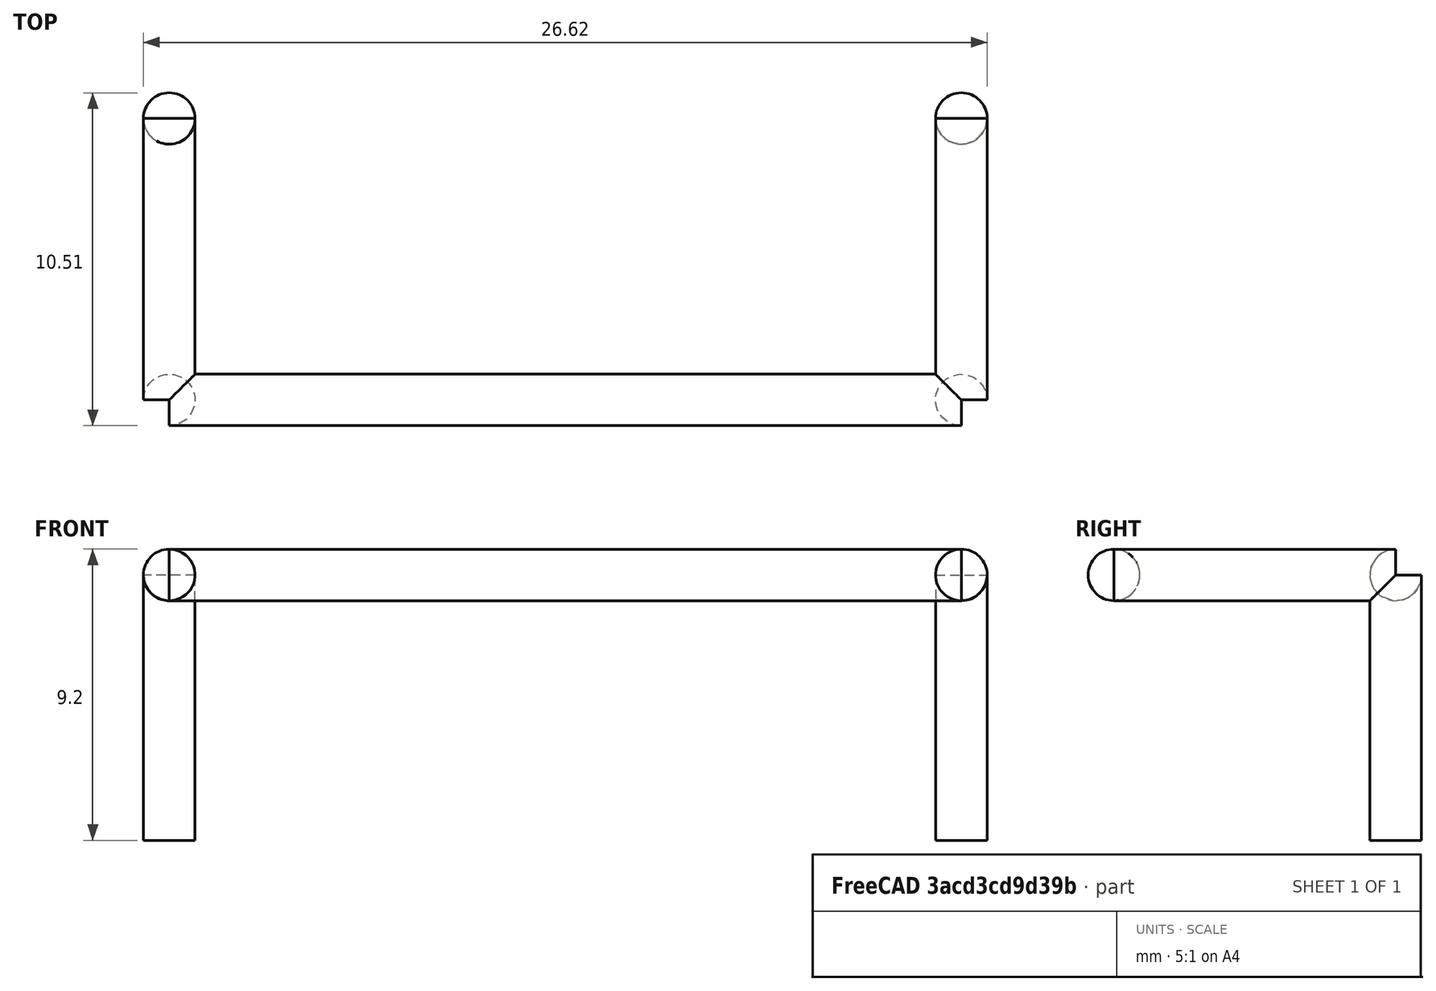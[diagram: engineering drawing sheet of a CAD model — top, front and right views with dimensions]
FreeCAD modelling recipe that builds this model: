
FCSTD DOCUMENT  (FreeCAD 1.0R39319 (Git))
Label: Wire Jumper
License: All rights reserved
LicenseURL: https://en.wikipedia.org/wiki/All_rights_reserved
objects: Sketcher::SketchObject×3, PartDesign::Plane×1, PartDesign::SubShapeBinder×1, PartDesign::AdditivePipe×1, PartDesign::Body×1
note: 12 computed .brp shape members not serialized (recipe doc carries the construction recipe); baked Part::Feature solids carry a one-line shape summary decoded from their .brp

FEATURE [Sketcher::SketchObject] Sketch
  ArcFitTolerance = 1e-06
  AttachmentSupport = -> [XZ_Plane]
  FullyConstrained = true
  MakeInternals = false
  MapMode = 5
  Placement = pos=(0,0,0) rot=(1,0,0;1.5708rad)
  sketch-geometry (2):
    g0: LineSegment StartX=-12.5 StartY=0 StartZ=0 EndX=-12.5 EndY=8.382 EndZ=0
    g1: LineSegment StartX=12.5 StartY=1e-16 StartZ=0 EndX=12.5 EndY=8.382 EndZ=0
  constraints (7):
    c: PointOnObject(g0,g-1)
    c: Vertical(g0)
    c: Vertical(g1)
    c: Symmetric(g0,g1,g-2)
    c: Distance(g1,g0) = 25
    c: Equal(g1,g0)
    c: DistanceY(g1,g1) = 8.382
FEATURE [PartDesign::Plane] DatumPlane
  AttachmentOffset = pos=(0,0,8.382) rot=(0,0,1;0rad)
  AttachmentSupport = -> [XY_Plane]
  Length = 60
  MapMode = 5
  Placement = pos=(0,0,8.382) rot=(0,0,1;0rad)
  ResizeMode = 0
  Width = 60
FEATURE [Sketcher::SketchObject] Sketch001
  ArcFitTolerance = 1e-06
  AttachmentSupport = -> [DatumPlane]
  FullyConstrained = true
  MakeInternals = false
  MapMode = 5
  Placement = pos=(0,0,8.382) rot=(0,0,1;0rad)
  sketch-geometry (3):
    g0: LineSegment StartX=-12.5 StartY=0 StartZ=0 EndX=-12.5 EndY=-8.89 EndZ=0
    g1: LineSegment StartX=-12.5 StartY=-8.89 StartZ=0 EndX=12.5 EndY=-8.89 EndZ=0
    g2: LineSegment StartX=12.5 StartY=-8.89 StartZ=0 EndX=12.5 EndY=0 EndZ=0
  constraints (9):
    c: PointOnObject(g0,g-1)
    c: Vertical(g0)
    c: Coincident(g1,g0)
    c: Coincident(g2,g1)
    c: Vertical(g2)
    c: PointOnObject(g2,g-1)
    c: Symmetric(g1,g0,g-2)
    c: DistanceX(g1,g1) = 25
    c: DistanceY(g2,g2) = 8.89
FEATURE [Sketcher::SketchObject] Sketch002
  ArcFitTolerance = 1e-06
  AttachmentSupport = -> [XY_Plane]
  FullyConstrained = true
  MakeInternals = false
  MapMode = 5
  sketch-geometry (1):
    g0: Circle CenterX=-12.5 CenterY=0 CenterZ=0 NormalX=0 NormalY=0 NormalZ=1 AngleXU=0 Radius=0.814
  constraints (3):
    c: PointOnObject(g0,g-1)
    c: Distance(g0,g-2) = 12.5
    c: Diameter(g0) = 1.628
FEATURE [PartDesign::SubShapeBinder] Binder
  BindCopyOnChange = 0
  BindMode = 0
  ClaimChildren = false
  Context = -> Body [Binder.]
  Fuse = false
  MakeFace = true
  OffsetFill = false
  OffsetIntersection = false
  OffsetJoinType = 0
  OffsetOpenResult = false
  PartialLoad = false
  Refine = true
  Relative = true
  Support = -> [Sketch001,Sketch]
  _Version = 2
FEATURE [PartDesign::AdditivePipe] AdditivePipe
  AuxilleryCurvelinear = true
  AuxillerySpineTangent = false
  Binormal = (0,0,0)
  Mode = 0
  Profile = -> Sketch002
  Refine = true
  Spine = -> Binder
  SpineTangent = false
  Suppressed = false
  Transformation = 0
  Transition = 2
FEATURE [PartDesign::Body] Body  label="Wire Body"
  AllowCompound = false
  Group = -> [Sketch,DatumPlane,Sketch001,Sketch002,Binder,AdditivePipe]
  Origin = -> Origin
  Tip = -> AdditivePipe
